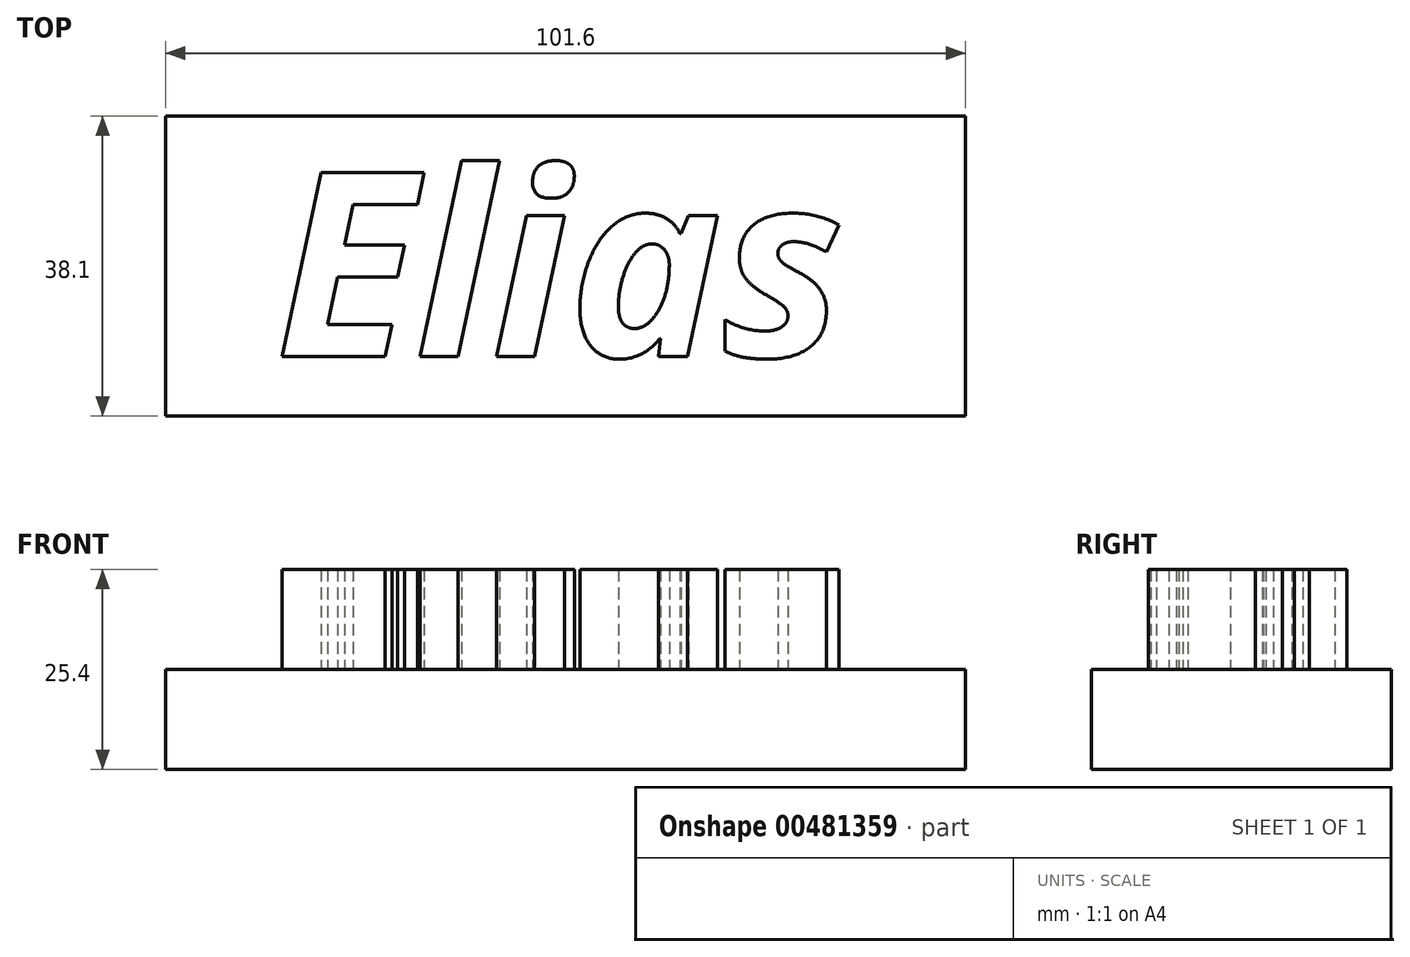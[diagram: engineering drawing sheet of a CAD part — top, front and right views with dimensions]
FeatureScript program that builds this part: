
annotation { "Feature Type Name" : "Feature", "Feature Type Description" : "" }
export const myFeature = defineFeature(function(context is Context, id is Id, definition is map)
    precondition{}
    {
        {
            var Q0;
            Q0=qCreatedBy(makeId("Top.planeOp"),FACE);
            var sketch = newSketch(context, id + "F0", { "sketchPlane" : qUnion([Q0])});
            skLineSegment(sketch, "E0.bottom", {"start": v(-50.8, -19.05) * mm, "end": v(50.8, -19.05) * mm});
            skLineSegment(sketch, "E0.top", {"start": v(-50.8, 19.05) * mm, "end": v(50.8, 19.05) * mm});
            skLineSegment(sketch, "E0.left", {"start": v(-50.8, -19.05) * mm, "end": v(-50.8, 19.05) * mm});
            skLineSegment(sketch, "E0.right", {"start": v(50.8, -19.05) * mm, "end": v(50.8, 19.05) * mm});
            skPoint(sketch, "E0.middle", {"position": v(0, 0) * mm});
            skSolve(sketch);
        }
        {
            var Q0;
            Q0 = qSketchRegion(id + "F0", true);
            extrude(context, id + "F1", {"entities" : qUnion([Q0]), "depth" : 12.7 * mm});
        }
        {
            var Q0;
            Q0=makeQuery(id+"F1.opExtrude","CAP_FACE",FACE,{"disambiguationData":[OSD([sQuery(id+"F0.wireOp",EDGE,"E0.bottom"),sQuery(id+"F0.wireOp",EDGE,"E0.top"),sQuery(id+"F0.wireOp",EDGE,"E0.left"),sQuery(id+"F0.wireOp",EDGE,"E0.right")])],"isStart":false});
            var sketch = newSketch(context, id + "F2", { "sketchPlane" : qUnion([Q0])});
            skText(sketch, "E1", { "text": "Elias", "fontName": "OpenSans-BoldItalic.ttf"});
            const initialGuessF2  = {"E1": [-0.03684, -0.01151, 1, 0, 0.0236]};
            skSetInitialGuess(sketch, initialGuessF2);
            skSolve(sketch);
        }
        {
            var Q0;
            Q0 = qSketchRegion(id + "F2", true);
            extrude(context, id + "F3", {"entities" : qUnion([Q0]), "operationType" : NewBodyOperationType.ADD, "depth" : 12.7 * mm});
        }
    });
